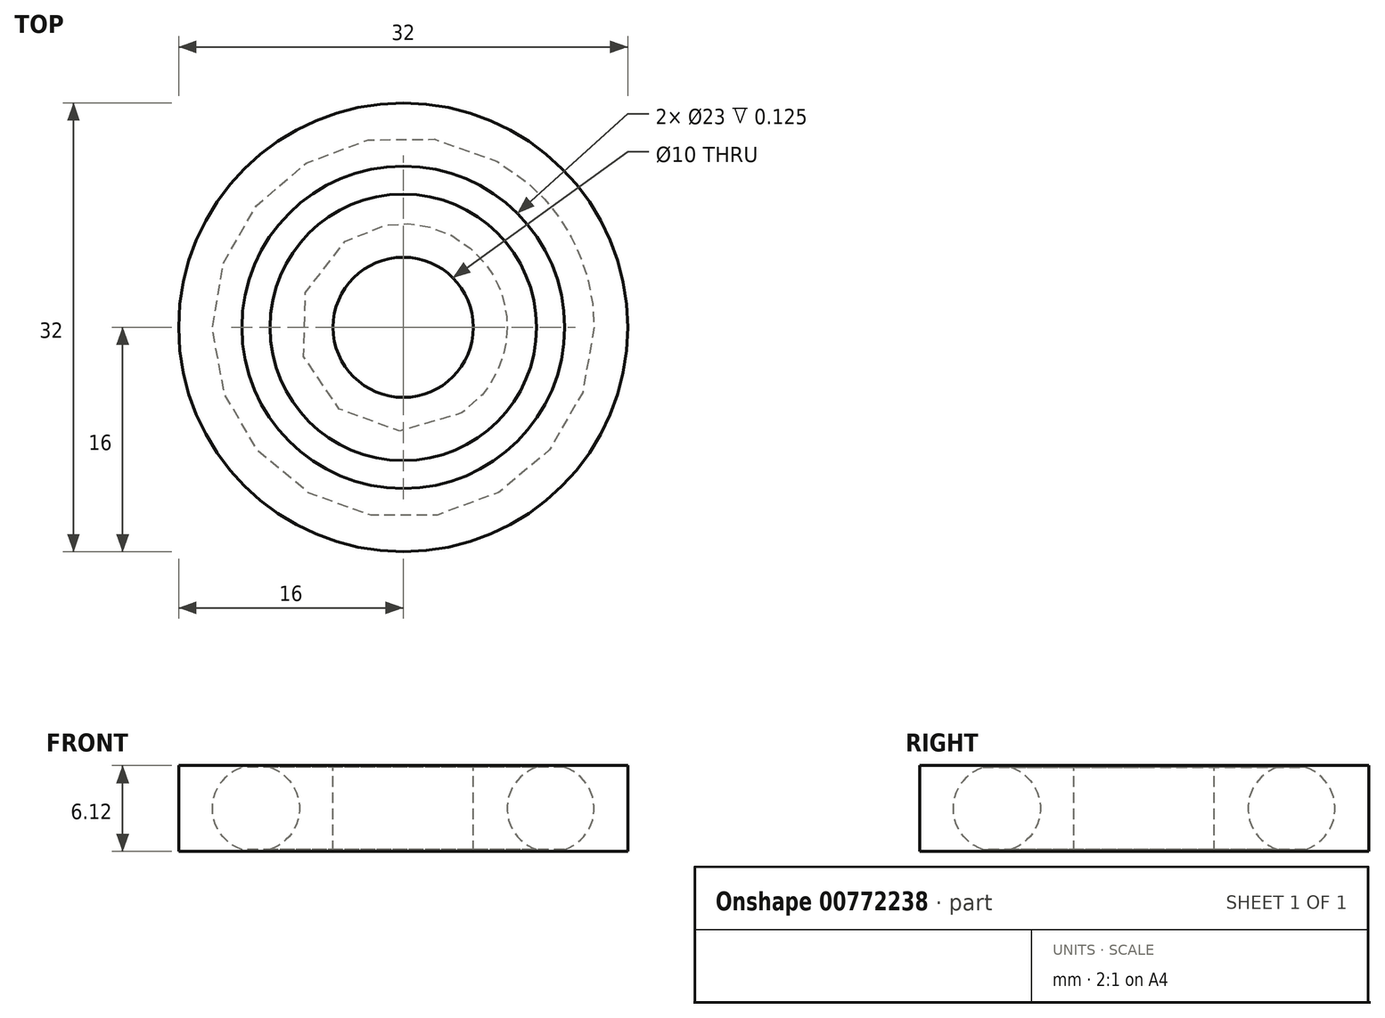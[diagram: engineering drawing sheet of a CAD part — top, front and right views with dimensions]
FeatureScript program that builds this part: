
annotation { "Feature Type Name" : "Feature", "Feature Type Description" : "" }
export const myFeature = defineFeature(function(context is Context, id is Id, definition is map)
    precondition{}
    {
        {
            var Q0;
            Q0=qCreatedBy(makeId("Front.planeOp"),FACE);
            var sketch = newSketch(context, id + "F0", { "sketchPlane" : qUnion([Q0])});
            skCircle(sketch, "E0", {"center": v(0, 0) * mm, "radius": 3.1 * mm});
            skLineSegment(sketch, "E1.bottom", {"start": v(0.5, 4.09) * mm, "end": v(-0.5, 4.09) * mm});
            skLineSegment(sketch, "E1.top", {"start": v(0.5, -4.09) * mm, "end": v(-0.5, -4.09) * mm});
            skLineSegment(sketch, "E1.left", {"start": v(0.5, 4.09) * mm, "end": v(0.5, -4.09) * mm});
            skLineSegment(sketch, "E1.right", {"start": v(-0.5, 4.09) * mm, "end": v(-0.5, -4.09) * mm});
            skPoint(sketch, "E2", {"position": v(-0.5, 3.06) * mm});
            skPoint(sketch, "E3", {"position": v(0.5, 3.06) * mm});
            skPoint(sketch, "E4", {"position": v(0.5, -3.06) * mm});
            skPoint(sketch, "E5", {"position": v(-0.5, -3.06) * mm});
            skLineSegment(sketch, "E6.bottom", {"start": v(0.5, 3.06) * mm, "end": v(10.5, 3.06) * mm});
            skLineSegment(sketch, "E6.top", {"start": v(0.5, -3.06) * mm, "end": v(10.5, -3.06) * mm});
            skLineSegment(sketch, "E6.left", {"start": v(0.5, 3.06) * mm, "end": v(0.5, -3.06) * mm});
            skLineSegment(sketch, "E6.right", {"start": v(10.5, 3.06) * mm, "end": v(10.5, -3.06) * mm});
            skLineSegment(sketch, "E7.bottom", {"start": v(-0.5, 3.06) * mm, "end": v(-5.5, 3.06) * mm});
            skLineSegment(sketch, "E7.top", {"start": v(-0.5, -3.06) * mm, "end": v(-5.5, -3.06) * mm});
            skLineSegment(sketch, "E7.left", {"start": v(-0.5, 3.06) * mm, "end": v(-0.5, -3.06) * mm});
            skLineSegment(sketch, "E7.right", {"start": v(-5.5, 3.06) * mm, "end": v(-5.5, -3.06) * mm});
            skLineSegment(sketch, "E8", {"start": v(-0.5, 3.06) * mm, "end": v(-1, 3.06) * mm, "construction": true});
            skLineSegment(sketch, "E9", {"start": v(0.5, 3.06) * mm, "end": v(1, 3.06) * mm, "construction": true});
            skLineSegment(sketch, "E10", {"start": v(-1, 3.06) * mm, "end": v(-1, -3.06) * mm});
            skLineSegment(sketch, "E11", {"start": v(1, 3.06) * mm, "end": v(1, -3.06) * mm});
            skSolve(sketch);
        }
        {
            var Q0;
            {var subQ0=sQuery(id+"F0.wireOp",EDGE,"E6.right");Q0=makeQuery(id+"F0.imprint","IMPRINT",FACE,{"disambiguationData":[TD([[makeQuery(id+"F0.imprint","IMPRINT",EDGE,{"derivedFrom":subQ0}),-1.0]])]});}
            var Q1;
            Q1=sQuery(id+"F0.wireOp",EDGE,"E6.right");
            revolve(context, id + "F1", {"surfaceOperationType" : NewSurfaceOperationType.NEW, "entities" : qUnion([Q0]), "axis" : qUnion([Q1]), "revolveType" : RevolveType.FULL});
        }
        {
            var Q0;
            {var subQ0=sQuery(id+"F0.wireOp",EDGE,"E7.right");Q0=makeQuery(id+"F0.imprint","IMPRINT",FACE,{"disambiguationData":[TD([[makeQuery(id+"F0.imprint","IMPRINT",EDGE,{"derivedFrom":subQ0}),1.0]])]});}
            var Q1;
            Q1=sQuery(id+"F0.wireOp",EDGE,"E6.right");
            revolve(context, id + "F2", {"surfaceOperationType" : NewSurfaceOperationType.NEW, "entities" : qUnion([Q0]), "axis" : qUnion([Q1]), "revolveType" : RevolveType.FULL});
        }
        {
            var Q0;
            Q0=makeQuery(id+"F1.opRevolve","SWEPT_FACE",FACE,{"disambiguationData":[OSD([sQuery(id+"F0.wireOp",EDGE,"E6.bottom")])]});
            var sketch = newSketch(context, id + "F3", { "sketchPlane" : qUnion([Q0])});
            skPoint(sketch, "E12", {"position": v(10.5, 0) * mm});
            skSolve(sketch);
        }
        {
            var Q0;
            Q0=sQuery(id+"F3.wireOp",VERTEX,"E12");
            var Q1;
            Q1=makeQuery(id+"F1.opRevolve","SWEPT_BODY",BODY,{"disambiguationData":[OSD([sQuery(id+"F0.wireOp",EDGE,"E0"),sQuery(id+"F0.wireOp",EDGE,"E6.bottom"),sQuery(id+"F0.wireOp",EDGE,"E6.top"),sQuery(id+"F0.wireOp",EDGE,"E6.right")])]});
            hole(context, id + "F4", {"style" : HoleStyle.SIMPLE, "endStyle" : HoleEndStyle.THROUGH, "holeDiameter" : 10 * mm, "majorDiameter" : 5 * mm, "isTappedThrough" : true, "tappedDepth" : 12 * mm, "tapClearance" : 3, "startFromSketch" : true, "locations" : qUnion([Q0]), "scope" : qUnion([Q1])});
        }
    });
